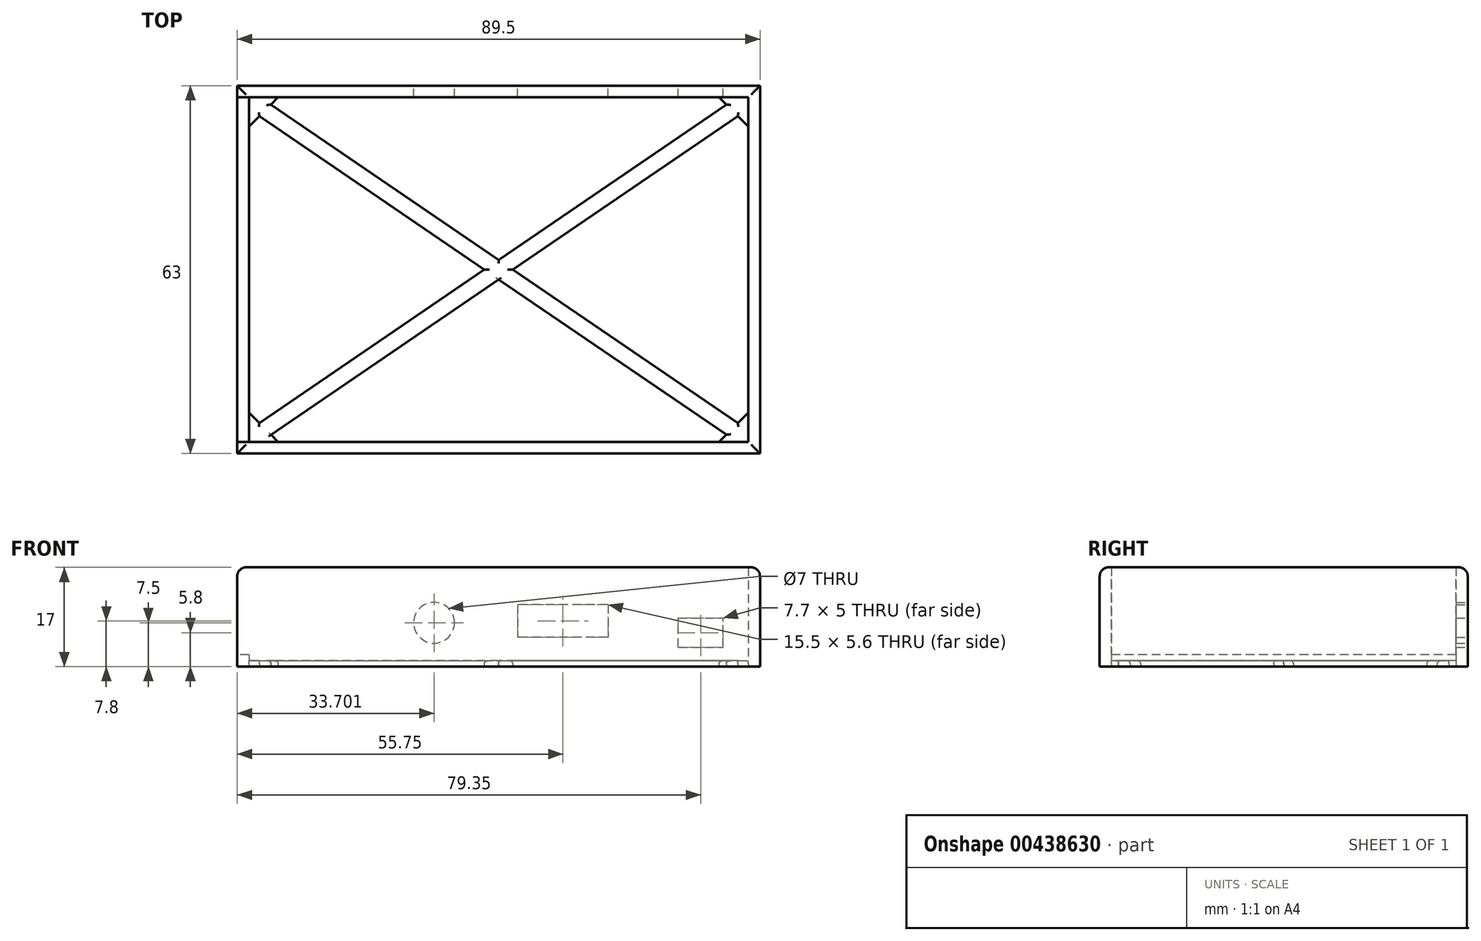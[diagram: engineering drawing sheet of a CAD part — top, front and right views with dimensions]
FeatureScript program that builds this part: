
annotation { "Feature Type Name" : "Feature", "Feature Type Description" : "" }
export const myFeature = defineFeature(function(context is Context, id is Id, definition is map)
    precondition{}
    {
        {
            var Q0;
            Q0=qCreatedBy(makeId("Top.planeOp"),FACE);
            var sketch = newSketch(context, id + "F0", { "sketchPlane" : qUnion([Q0])});
            skLineSegment(sketch, "E0.bottom", {"start": v(-42.75, 29.5) * mm, "end": v(42.75, 29.5) * mm});
            skLineSegment(sketch, "E0.top", {"start": v(-42.75, -29.5) * mm, "end": v(42.75, -29.5) * mm});
            skLineSegment(sketch, "E0.left", {"start": v(-42.75, 29.5) * mm, "end": v(-42.75, -29.5) * mm});
            skLineSegment(sketch, "E0.right", {"start": v(42.75, 29.5) * mm, "end": v(42.75, -29.5) * mm});
            skPoint(sketch, "E0.middle", {"position": v(0, 0) * mm});
            skLineSegment(sketch, "E1.bottom", {"start": v(-44.75, 31.5) * mm, "end": v(44.75, 31.5) * mm});
            skLineSegment(sketch, "E1.top", {"start": v(-44.75, -31.5) * mm, "end": v(44.75, -31.5) * mm});
            skLineSegment(sketch, "E1.left", {"start": v(-44.75, 31.5) * mm, "end": v(-44.75, -31.5) * mm});
            skLineSegment(sketch, "E1.right", {"start": v(44.75, 31.5) * mm, "end": v(44.75, -31.5) * mm});
            skLineSegment(sketch, "E2", {"start": v(-40.97, 26.28) * mm, "end": v(-2.46, 0) * mm});
            skLineSegment(sketch, "E3", {"start": v(40.97, -26.28) * mm, "end": v(2.45, 0) * mm});
            skLineSegment(sketch, "E4", {"start": v(38.97, 28.28) * mm, "end": v(-0.01, 1.67) * mm});
            skLineSegment(sketch, "E5", {"start": v(-38.97, -28.28) * mm, "end": v(0, -1.68) * mm});
            skLineSegment(sketch, "E6", {"start": v(-42.75, 27.5) * mm, "end": v(-42.75, 29.5) * mm, "construction": true});
            skLineSegment(sketch, "E7", {"start": v(-42.75, -29.5) * mm, "end": v(-42.75, -27.5) * mm, "construction": true});
            skLineSegment(sketch, "E8", {"start": v(-42.75, -29.5) * mm, "end": v(-40.75, -29.5) * mm, "construction": true});
            skLineSegment(sketch, "E9", {"start": v(40.75, -29.5) * mm, "end": v(42.75, -29.5) * mm, "construction": true});
            skLineSegment(sketch, "E10", {"start": v(42.75, -29.5) * mm, "end": v(42.75, -27.5) * mm, "construction": true});
            skLineSegment(sketch, "E11", {"start": v(42.75, 27.5) * mm, "end": v(42.75, 29.5) * mm, "construction": true});
            skLineSegment(sketch, "E12", {"start": v(42.75, 29.5) * mm, "end": v(40.75, 29.5) * mm, "construction": true});
            skLineSegment(sketch, "E13.trimOffspring", {"start": v(0, -1.68) * mm, "end": v(38.97, -28.28) * mm});
            skLineSegment(sketch, "E14.trimOffspring", {"start": v(2.45, 0) * mm, "end": v(40.97, 26.28) * mm});
            skLineSegment(sketch, "E15.trimOffspring", {"start": v(-0.01, 1.67) * mm, "end": v(-38.99, 28.26) * mm});
            skLineSegment(sketch, "E16.trimOffspring", {"start": v(-2.46, 0) * mm, "end": v(-40.97, -26.28) * mm});
            skLineSegment(sketch, "E17", {"start": v(37.75, 29.5) * mm, "end": v(42.75, 24.5) * mm});
            skLineSegment(sketch, "E18.MirrorCS", {"start": v(-37.75, 29.5) * mm, "end": v(-42.75, 24.5) * mm});
            skLineSegment(sketch, "E19.MirrorCS", {"start": v(37.75, -29.5) * mm, "end": v(42.75, -24.5) * mm});
            skLineSegment(sketch, "E20.MirrorCS", {"start": v(-37.75, -29.5) * mm, "end": v(-42.75, -24.5) * mm});
            skSolve(sketch);
        }
        {
            var Q0;
            Q0=makeQuery(id+"F0.imprint","IMPRINT",FACE,{"disambiguationData":[TD([[makeQuery(id+"F0.imprint","IMPRINT",EDGE,{"derivedFrom":sQuery(id+"F0.wireOp",EDGE,"E0.bottom")}),1.0]])]});
            extrude(context, id + "F1", {"entities" : qUnion([Q0]), "depth" : 17 * mm});
        }
        {
            var Q0;
            {var subQ6=sQuery(id+"F0.wireOp",EDGE,"E2");Q0=makeQuery(id+"F0.imprint","IMPRINT",FACE,{"disambiguationData":[TD([[makeQuery(id+"F0.imprint","IMPRINT",EDGE,{"derivedFrom":subQ6}),1.0]])]});}
            var Q1;
            {var subQ3=sQuery(id+"F0.wireOp",EDGE,"E0.left");var subQ4=sQuery(id+"F0.wireOp",EDGE,"E0.bottom");var subQ5=makeQuery(id+"F0.imprint","INTERSECT",VERTEX,{"derivedFrom":[subQ4,subQ3]});Q1=makeQuery(id+"F0.imprint","IMPRINT",FACE,{"disambiguationData":[TD([[makeQuery(id+"F0.imprint","IMPRINT",EDGE,{"disambiguationData":[TD([[subQ5,-1.0]])],"derivedFrom":subQ4}),-1.0]])]});}
            var Q2;
            {var subQ3=sQuery(id+"F0.wireOp",EDGE,"E0.bottom");var subQ5=sQuery(id+"F0.wireOp",EDGE,"E0.right");var subQ6=makeQuery(id+"F0.imprint","INTERSECT",VERTEX,{"derivedFrom":[subQ3,subQ5]});Q2=makeQuery(id+"F0.imprint","IMPRINT",FACE,{"disambiguationData":[TD([[makeQuery(id+"F0.imprint","IMPRINT",EDGE,{"disambiguationData":[TD([[subQ6,1.0]])],"derivedFrom":subQ3}),-1.0]])]});}
            var Q3;
            {var subQ3=sQuery(id+"F0.wireOp",EDGE,"E0.right");var subQ4=sQuery(id+"F0.wireOp",EDGE,"E0.top");var subQ5=makeQuery(id+"F0.imprint","INTERSECT",VERTEX,{"derivedFrom":[subQ4,subQ3]});Q3=makeQuery(id+"F0.imprint","IMPRINT",FACE,{"disambiguationData":[TD([[makeQuery(id+"F0.imprint","IMPRINT",EDGE,{"disambiguationData":[TD([[subQ5,1.0]])],"derivedFrom":subQ4}),1.0]])]});}
            var Q4;
            {var subQ3=sQuery(id+"F0.wireOp",EDGE,"E0.top");var subQ5=sQuery(id+"F0.wireOp",EDGE,"E0.left");var subQ6=makeQuery(id+"F0.imprint","INTERSECT",VERTEX,{"derivedFrom":[subQ3,subQ5]});Q4=makeQuery(id+"F0.imprint","IMPRINT",FACE,{"disambiguationData":[TD([[makeQuery(id+"F0.imprint","IMPRINT",EDGE,{"disambiguationData":[TD([[subQ6,-1.0]])],"derivedFrom":subQ3}),1.0]])]});}
            extrude(context, id + "F2", {"entities" : qUnion([Q0, Q1, Q2, Q3, Q4]), "operationType" : NewBodyOperationType.ADD, "depth" : 1 * mm});
        }
        {
            var Q0;
            Q0=makeQuery(id+"F1.opExtrude","CAP_EDGE",EDGE,{"disambiguationData":[OSD([sQuery(id+"F0.wireOp",EDGE,"E1.bottom")])],"isStart":false});
            var Q1;
            Q1=makeQuery(id+"F1.opExtrude","CAP_EDGE",EDGE,{"disambiguationData":[OSD([sQuery(id+"F0.wireOp",EDGE,"E1.left")])],"isStart":false});
            var Q2;
            Q2=makeQuery(id+"F1.opExtrude","CAP_EDGE",EDGE,{"disambiguationData":[OSD([sQuery(id+"F0.wireOp",EDGE,"E1.top")])],"isStart":false});
            var Q3;
            Q3=makeQuery(id+"F1.opExtrude","CAP_EDGE",EDGE,{"disambiguationData":[OSD([sQuery(id+"F0.wireOp",EDGE,"E1.right")])],"isStart":false});
            fillet(context, id + "F3", {"entities" : qUnion([Q0, Q1, Q2, Q3]), "radius" : 1.5 * mm, "tangentPropagation" : true, "allowEdgeOverflow" : false});
        }
        {
            var Q0;
            Q0=makeQuery(id+"F2.opExtrude","CAP_EDGE",EDGE,{"disambiguationData":[OSD([sQuery(id+"F0.wireOp",EDGE,"E15.trimOffspring")])],"isStart":false});
            var Q1;
            Q1=makeQuery(id+"F2.opExtrude","CAP_EDGE",EDGE,{"disambiguationData":[OSD([sQuery(id+"F0.wireOp",EDGE,"E2")])],"isStart":false});
            var Q2;
            Q2=makeQuery(id+"F2.opExtrude","CAP_EDGE",EDGE,{"disambiguationData":[OSD([sQuery(id+"F0.wireOp",EDGE,"E4")])],"isStart":false});
            var Q3;
            Q3=makeQuery(id+"F2.opExtrude","CAP_EDGE",EDGE,{"disambiguationData":[OSD([sQuery(id+"F0.wireOp",EDGE,"E14.trimOffspring")])],"isStart":false});
            var Q4;
            Q4=makeQuery(id+"F2.opExtrude","CAP_EDGE",EDGE,{"disambiguationData":[OSD([sQuery(id+"F0.wireOp",EDGE,"E16.trimOffspring")])],"isStart":false});
            var Q5;
            Q5=makeQuery(id+"F2.opExtrude","CAP_EDGE",EDGE,{"disambiguationData":[OSD([sQuery(id+"F0.wireOp",EDGE,"E5")])],"isStart":true});
            var Q6;
            Q6=makeQuery(id+"F2.opExtrude","CAP_EDGE",EDGE,{"disambiguationData":[OSD([sQuery(id+"F0.wireOp",EDGE,"E13.trimOffspring")])],"isStart":false});
            var Q7;
            Q7=makeQuery(id+"F2.opExtrude","CAP_EDGE",EDGE,{"disambiguationData":[OSD([sQuery(id+"F0.wireOp",EDGE,"E3")])],"isStart":false});
            var Q8;
            {var subQ0=sQuery(id+"F0.wireOp",EDGE,"E18.MirrorCS");Q8=makeQuery(id+"F2.opExtrude","CAP_EDGE",EDGE,{"disambiguationData":[OSD([subQ0]),TDD([makeQuery(id+"F0.imprint","IMPRINT",EDGE,{"disambiguationData":[TD([[makeQuery(id+"F0.imprint","INTERSECT",VERTEX,{"derivedFrom":[sQuery(id+"F0.wireOp",EDGE,"E2"),subQ0]}),-1.0]])],"derivedFrom":subQ0})])],"isStart":false});}
            var Q9;
            {var subQ0=sQuery(id+"F0.wireOp",EDGE,"E18.MirrorCS");Q9=makeQuery(id+"F2.opExtrude","CAP_EDGE",EDGE,{"disambiguationData":[OSD([subQ0]),TDD([makeQuery(id+"F0.imprint","IMPRINT",EDGE,{"disambiguationData":[TD([[makeQuery(id+"F0.imprint","INTERSECT",VERTEX,{"derivedFrom":[sQuery(id+"F0.wireOp",EDGE,"E15.trimOffspring"),subQ0]}),1.0]])],"derivedFrom":subQ0})])],"isStart":false});}
            var Q10;
            {var subQ0=sQuery(id+"F0.wireOp",EDGE,"E17");Q10=makeQuery(id+"F2.opExtrude","CAP_EDGE",EDGE,{"disambiguationData":[OSD([subQ0]),TDD([makeQuery(id+"F0.imprint","IMPRINT",EDGE,{"disambiguationData":[TD([[makeQuery(id+"F0.imprint","INTERSECT",VERTEX,{"derivedFrom":[sQuery(id+"F0.wireOp",EDGE,"E14.trimOffspring"),subQ0]}),-1.0]])],"derivedFrom":subQ0})])],"isStart":false});}
            var Q11;
            {var subQ0=sQuery(id+"F0.wireOp",EDGE,"E17");Q11=makeQuery(id+"F2.opExtrude","CAP_EDGE",EDGE,{"disambiguationData":[OSD([subQ0]),TDD([makeQuery(id+"F0.imprint","IMPRINT",EDGE,{"disambiguationData":[TD([[makeQuery(id+"F0.imprint","INTERSECT",VERTEX,{"derivedFrom":[sQuery(id+"F0.wireOp",EDGE,"E4"),subQ0]}),1.0]])],"derivedFrom":subQ0})])],"isStart":false});}
            var Q12;
            {var subQ0=sQuery(id+"F0.wireOp",EDGE,"E20.MirrorCS");Q12=makeQuery(id+"F2.opExtrude","CAP_EDGE",EDGE,{"disambiguationData":[OSD([subQ0]),TDD([makeQuery(id+"F0.imprint","IMPRINT",EDGE,{"disambiguationData":[TD([[makeQuery(id+"F0.imprint","INTERSECT",VERTEX,{"derivedFrom":[sQuery(id+"F0.wireOp",EDGE,"E16.trimOffspring"),subQ0]}),-1.0]])],"derivedFrom":subQ0})])],"isStart":false});}
            var Q13;
            {var subQ0=sQuery(id+"F0.wireOp",EDGE,"E20.MirrorCS");Q13=makeQuery(id+"F2.opExtrude","CAP_EDGE",EDGE,{"disambiguationData":[OSD([subQ0]),TDD([makeQuery(id+"F0.imprint","IMPRINT",EDGE,{"disambiguationData":[TD([[makeQuery(id+"F0.imprint","INTERSECT",VERTEX,{"derivedFrom":[sQuery(id+"F0.wireOp",EDGE,"E5"),subQ0]}),1.0]])],"derivedFrom":subQ0})])],"isStart":false});}
            var Q14;
            {var subQ0=sQuery(id+"F0.wireOp",EDGE,"E19.MirrorCS");Q14=makeQuery(id+"F2.opExtrude","CAP_EDGE",EDGE,{"disambiguationData":[OSD([subQ0]),TDD([makeQuery(id+"F0.imprint","IMPRINT",EDGE,{"disambiguationData":[TD([[makeQuery(id+"F0.imprint","INTERSECT",VERTEX,{"derivedFrom":[sQuery(id+"F0.wireOp",EDGE,"E3"),subQ0]}),-1.0]])],"derivedFrom":subQ0})])],"isStart":false});}
            var Q15;
            {var subQ0=sQuery(id+"F0.wireOp",EDGE,"E19.MirrorCS");Q15=makeQuery(id+"F2.opExtrude","CAP_EDGE",EDGE,{"disambiguationData":[OSD([subQ0]),TDD([makeQuery(id+"F0.imprint","IMPRINT",EDGE,{"disambiguationData":[TD([[makeQuery(id+"F0.imprint","INTERSECT",VERTEX,{"derivedFrom":[sQuery(id+"F0.wireOp",EDGE,"E13.trimOffspring"),subQ0]}),1.0]])],"derivedFrom":subQ0})])],"isStart":false});}
            fillet(context, id + "F4", {"entities" : qUnion([Q0, Q1, Q2, Q3, Q4, Q5, Q6, Q7, Q8, Q9, Q10, Q11, Q12, Q13, Q14, Q15]), "radius" : 0.5 * mm, "tangentPropagation" : true, "allowEdgeOverflow" : false});
        }
        {
            var Q0;
            Q0=makeQuery(id+"F1.opExtrude","SWEPT_FACE",FACE,{"disambiguationData":[OSD([sQuery(id+"F0.wireOp",EDGE,"E1.bottom")])]});
            var sketch = newSketch(context, id + "F5", { "sketchPlane" : qUnion([Q0])});
            skLineSegment(sketch, "E21.bottom", {"start": v(-18.75, 10.6) * mm, "end": v(-3.25, 10.6) * mm});
            skLineSegment(sketch, "E21.top", {"start": v(-18.75, 5) * mm, "end": v(-3.25, 5) * mm});
            skLineSegment(sketch, "E21.left", {"start": v(-18.75, 10.6) * mm, "end": v(-18.75, 5) * mm});
            skLineSegment(sketch, "E21.right", {"start": v(-3.25, 10.6) * mm, "end": v(-3.25, 5) * mm});
            skCircle(sketch, "E22", {"center": v(11.05, 7.5) * mm, "radius": 3.5 * mm});
            skLineSegment(sketch, "E23.bottom", {"start": v(-30.75, 3.3) * mm, "end": v(-38.45, 3.3) * mm});
            skLineSegment(sketch, "E23.top", {"start": v(-30.75, 8.3) * mm, "end": v(-38.45, 8.3) * mm});
            skLineSegment(sketch, "E23.left", {"start": v(-30.75, 3.3) * mm, "end": v(-30.75, 8.3) * mm});
            skLineSegment(sketch, "E23.right", {"start": v(-38.45, 3.3) * mm, "end": v(-38.45, 8.3) * mm});
            skSolve(sketch);
        }
        {
            var Q0;
            Q0=makeQuery(id+"F5.imprint","IMPRINT",FACE,{"disambiguationData":[TD([[makeQuery(id+"F5.imprint","IMPRINT",EDGE,{"derivedFrom":sQuery(id+"F5.wireOp",EDGE,"E23.bottom")}),-1.0]])]});
            var Q1;
            Q1=makeQuery(id+"F5.imprint","IMPRINT",FACE,{"disambiguationData":[TD([[makeQuery(id+"F5.imprint","IMPRINT",EDGE,{"derivedFrom":sQuery(id+"F5.wireOp",EDGE,"E21.bottom")}),-1.0]])]});
            var Q2;
            Q2=makeQuery(id+"F5.imprint","IMPRINT",FACE,{"disambiguationData":[TD([[makeQuery(id+"F5.imprint","IMPRINT",EDGE,{"derivedFrom":sQuery(id+"F5.wireOp",EDGE,"E22")}),1.0]])]});
            extrude(context, id + "F6", {"entities" : qUnion([Q0, Q1, Q2]), "operationType" : NewBodyOperationType.REMOVE, "oppositeDirection" : true, "depth" : 25 * mm});
        }
        {
            var Q0;
            Q0=makeQuery(id+"F1.opExtrude","SWEPT_FACE",FACE,{"disambiguationData":[OSD([sQuery(id+"F0.wireOp",EDGE,"E1.left")])]});
            var sketch = newSketch(context, id + "F7", { "sketchPlane" : qUnion([Q0])});
            skLineSegment(sketch, "E24.bottom", {"start": v(-29.5, 2) * mm, "end": v(29.5, 2) * mm});
            skLineSegment(sketch, "E24.top", {"start": v(-29.5, 19) * mm, "end": v(29.5, 19) * mm});
            skLineSegment(sketch, "E24.left", {"start": v(-29.5, 2) * mm, "end": v(-29.5, 19) * mm});
            skLineSegment(sketch, "E24.right", {"start": v(29.5, 2) * mm, "end": v(29.5, 19) * mm});
            skPoint(sketch, "E24.middle", {"position": v(0, 10.5) * mm});
            skSolve(sketch);
        }
        {
            var Q0;
            {var subQ0=sQuery(id+"F7.wireOp",EDGE,"E24.bottom");Q0=makeQuery(id+"F7.imprint","IMPRINT",FACE,{"disambiguationData":[TD([[makeQuery(id+"F7.imprint","IMPRINT",EDGE,{"derivedFrom":subQ0}),1.0]])]});}
            var Q1;
            {var subQ0=sQuery(id+"F7.wireOp",EDGE,"E24.top");Q1=makeQuery(id+"F7.imprint","IMPRINT",FACE,{"disambiguationData":[TD([[makeQuery(id+"F7.imprint","IMPRINT",EDGE,{"derivedFrom":subQ0}),-1.0]])]});}
            extrude(context, id + "F8", {"entities" : qUnion([Q0, Q1]), "operationType" : NewBodyOperationType.REMOVE, "oppositeDirection" : true, "depth" : 25 * mm});
        }
    });
